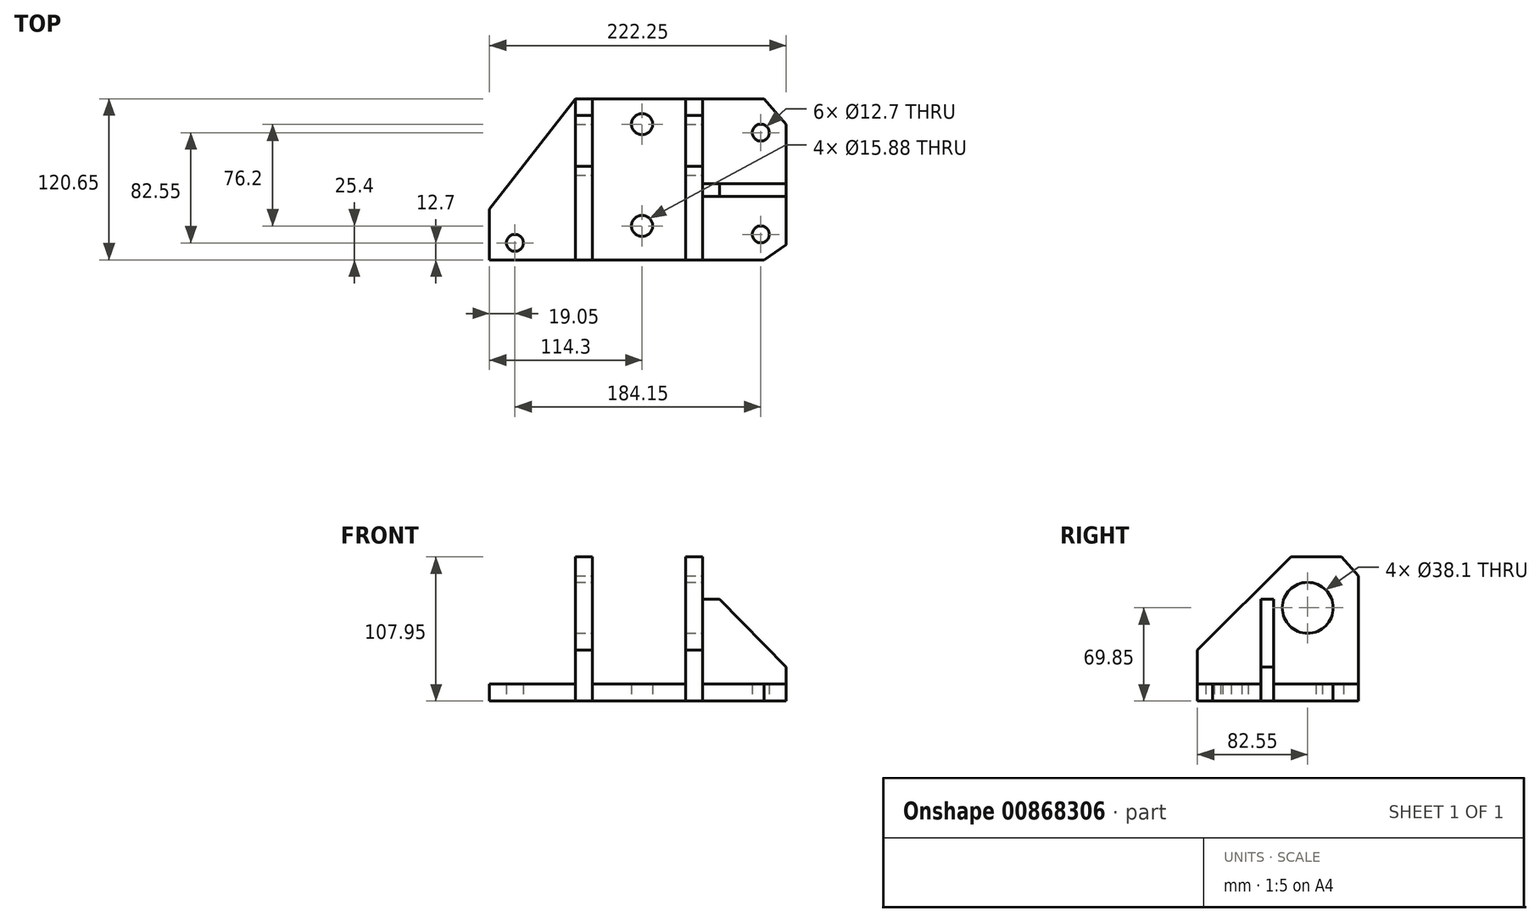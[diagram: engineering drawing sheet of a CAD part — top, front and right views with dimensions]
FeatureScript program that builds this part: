
annotation { "Feature Type Name" : "Feature", "Feature Type Description" : "" }
export const myFeature = defineFeature(function(context is Context, id is Id, definition is map)
    precondition{}
    {
        {
            var Q0;
            Q0=qCreatedBy(makeId("Top.planeOp"),FACE);
            var sketch = newSketch(context, id + "F0", { "sketchPlane" : qUnion([Q0])});
            skLineSegment(sketch, "E0", {"start": v(-91.37, 0) * mm, "end": v(91.5, 0) * mm});
            skLineSegment(sketch, "E1", {"start": v(91.5, 0) * mm, "end": v(107.95, 11.41) * mm});
            skLineSegment(sketch, "E2", {"start": v(107.95, 11.41) * mm, "end": v(107.95, 101.6) * mm});
            skLineSegment(sketch, "E3", {"start": v(107.95, 101.6) * mm, "end": v(91.5, 120.65) * mm});
            skLineSegment(sketch, "E4", {"start": v(91.5, 120.65) * mm, "end": v(-49.88, 120.65) * mm});
            skLineSegment(sketch, "E5", {"start": v(-49.88, 120.65) * mm, "end": v(-114.3, 38.1) * mm});
            skLineSegment(sketch, "E6", {"start": v(-114.3, 38.1) * mm, "end": v(-114.3, 0) * mm});
            skLineSegment(sketch, "E7", {"start": v(-114.3, 0) * mm, "end": v(-91.37, 0) * mm});
            skPoint(sketch, "E8.endSnap0", {"position": v(20.81, 120.65) * mm});
            skLineSegment(sketch, "E9", {"start": v(-49.88, 120.65) * mm, "end": v(-49.88, 0) * mm});
            skLineSegment(sketch, "E10", {"start": v(-37.18, 120.65) * mm, "end": v(-37.18, 0) * mm});
            skLineSegment(sketch, "E11", {"start": v(32.67, 120.65) * mm, "end": v(32.67, 0) * mm});
            skLineSegment(sketch, "E12", {"start": v(45.37, 120.65) * mm, "end": v(45.37, 0) * mm});
            skLineSegment(sketch, "E13", {"start": v(45.37, 47.63) * mm, "end": v(107.95, 47.63) * mm});
            skCircle(sketch, "E14", {"center": v(-95.25, 12.7) * mm, "radius": 6.35 * mm});
            skCircle(sketch, "E15", {"center": v(0, 25.4) * mm, "radius": 7.94 * mm});
            skCircle(sketch, "E16", {"center": v(0, 101.6) * mm, "radius": 7.94 * mm});
            skCircle(sketch, "E17", {"center": v(88.9, 19.05) * mm, "radius": 6.35 * mm});
            skCircle(sketch, "E18", {"center": v(88.9, 95.25) * mm, "radius": 6.35 * mm});
            skLineSegment(sketch, "E19", {"start": v(45.37, 57.15) * mm, "end": v(107.95, 57.15) * mm});
            skSolve(sketch);
        }
        {
            var Q0;
            {var subQ4=sQuery(id+"F0.wireOp",EDGE,"E3");Q0=makeQuery(id+"F0.imprint","IMPRINT",FACE,{"disambiguationData":[TD([[makeQuery(id+"F0.imprint","IMPRINT",EDGE,{"derivedFrom":subQ4}),1.0]])]});}
            var Q1;
            {var subQ5=sQuery(id+"F0.wireOp",EDGE,"E1");Q1=makeQuery(id+"F0.imprint","IMPRINT",FACE,{"disambiguationData":[TD([[makeQuery(id+"F0.imprint","IMPRINT",EDGE,{"derivedFrom":subQ5}),1.0]])]});}
            var Q2;
            {var subQ1=sQuery(id+"F0.wireOp",EDGE,"E10");Q2=makeQuery(id+"F0.imprint","IMPRINT",FACE,{"disambiguationData":[TD([[makeQuery(id+"F0.imprint","IMPRINT",EDGE,{"derivedFrom":subQ1}),1.0]])]});}
            var Q3;
            Q3=makeQuery(id+"F0.imprint","IMPRINT",FACE,{"disambiguationData":[TD([[makeQuery(id+"F0.imprint","IMPRINT",EDGE,{"derivedFrom":sQuery(id+"F0.wireOp",EDGE,"E5")}),1.0]])]});
            extrude(context, id + "F1", {"entities" : qUnion([Q0, Q1, Q2, Q3]), "depth" : 12.7 * mm, "offsetDistance" : 25.4 * mm});
        }
        {
            var Q0;
            {var subQ0=sQuery(id+"F0.wireOp",EDGE,"E9");Q0=makeQuery(id+"F0.imprint","IMPRINT",FACE,{"disambiguationData":[TD([[makeQuery(id+"F0.imprint","IMPRINT",EDGE,{"derivedFrom":subQ0}),1.0]])]});}
            var Q1;
            {var subQ4=sQuery(id+"F0.wireOp",EDGE,"E11");Q1=makeQuery(id+"F0.imprint","IMPRINT",FACE,{"disambiguationData":[TD([[makeQuery(id+"F0.imprint","IMPRINT",EDGE,{"derivedFrom":subQ4}),1.0]])]});}
            extrude(context, id + "F2", {"entities" : qUnion([Q0, Q1]), "depth" : 107.95 * mm, "offsetDistance" : 25.4 * mm});
        }
        {
            var Q0;
            {var subQ0=sQuery(id+"F0.wireOp",EDGE,"E13");Q0=makeQuery(id+"F0.imprint","IMPRINT",FACE,{"disambiguationData":[TD([[makeQuery(id+"F0.imprint","IMPRINT",EDGE,{"derivedFrom":subQ0}),1.0]])]});}
            extrude(context, id + "F3", {"entities" : qUnion([Q0]), "depth" : 76.2 * mm, "offsetDistance" : 25.4 * mm});
        }
        {
            var Q0;
            Q0=makeQuery(id+"F3.opExtrude","SWEPT_FACE",FACE,{"disambiguationData":[OSD([sQuery(id+"F0.wireOp",EDGE,"E19")])]});
            var sketch = newSketch(context, id + "F4", { "sketchPlane" : qUnion([Q0])});
            skLineSegment(sketch, "E20", {"start": v(-107.95, 12.7) * mm, "end": v(-107.95, 25.4) * mm});
            skLineSegment(sketch, "E21", {"start": v(-107.95, 25.4) * mm, "end": v(-58.07, 76.2) * mm});
            skLineSegment(sketch, "E22", {"start": v(-58.07, 76.2) * mm, "end": v(-45.37, 76.2) * mm});
            skSolve(sketch);
        }
        {
            var Q0;
            {var subQ0=sQuery(id+"F4.wireOp",EDGE,"E21");Q0=makeQuery(id+"F4.imprint","IMPRINT",FACE,{"disambiguationData":[TD([[makeQuery(id+"F4.imprint","IMPRINT",EDGE,{"derivedFrom":subQ0}),1.0]])]});}
            extrude(context, id + "F5", {"entities" : qUnion([Q0]), "operationType" : NewBodyOperationType.REMOVE, "oppositeDirection" : true, "depth" : 25.4 * mm, "offsetDistance" : 25.4 * mm});
        }
        {
            var Q0;
            Q0=makeQuery(id+"F2.opExtrude","SWEPT_FACE",FACE,{"disambiguationData":[OSD([sQuery(id+"F0.wireOp",EDGE,"E12")])]});
            var sketch = newSketch(context, id + "F6", { "sketchPlane" : qUnion([Q0])});
            skLineSegment(sketch, "E23", {"start": v(0, 12.7) * mm, "end": v(0, 38.1) * mm});
            skLineSegment(sketch, "E24", {"start": v(0, 38.1) * mm, "end": v(69.91, 107.95) * mm});
            skLineSegment(sketch, "E25", {"start": v(69.91, 107.95) * mm, "end": v(108.01, 107.95) * mm});
            skLineSegment(sketch, "E26", {"start": v(108.01, 107.95) * mm, "end": v(120.65, 93.7) * mm});
            skLineSegment(sketch, "E27", {"start": v(120.65, 93.7) * mm, "end": v(120.65, 12.7) * mm});
            skCircle(sketch, "E28", {"center": v(82.55, 69.85) * mm, "radius": 19.05 * mm});
            skSolve(sketch);
        }
        {
            var Q0;
            {var subQ0=sQuery(id+"F6.wireOp",EDGE,"E24");Q0=makeQuery(id+"F6.imprint","IMPRINT",FACE,{"disambiguationData":[TD([[makeQuery(id+"F6.imprint","IMPRINT",EDGE,{"derivedFrom":subQ0}),1.0]])]});}
            var Q1;
            {var subQ0=sQuery(id+"F6.wireOp",EDGE,"E26");Q1=makeQuery(id+"F6.imprint","IMPRINT",FACE,{"disambiguationData":[TD([[makeQuery(id+"F6.imprint","IMPRINT",EDGE,{"derivedFrom":subQ0}),1.0]])]});}
            var Q2;
            Q2=makeQuery(id+"F6.imprint","IMPRINT",FACE,{"disambiguationData":[TD([[makeQuery(id+"F6.imprint","IMPRINT",EDGE,{"derivedFrom":sQuery(id+"F6.wireOp",EDGE,"E28")}),1.0]])]});
            extrude(context, id + "F7", {"entities" : qUnion([Q0, Q1, Q2]), "operationType" : NewBodyOperationType.REMOVE, "endBound" : BoundingType.THROUGH_ALL, "oppositeDirection" : true, "depth" : 25.4 * mm, "offsetDistance" : 25.4 * mm});
        }
    });
